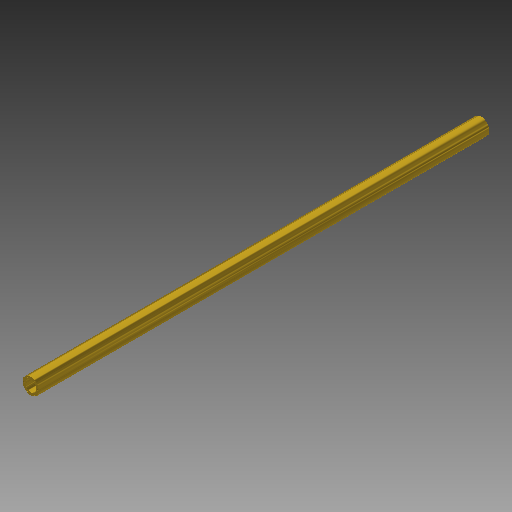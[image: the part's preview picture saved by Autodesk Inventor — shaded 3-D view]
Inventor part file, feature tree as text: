
AUTODESK INVENTOR PART (.ipt)
format: ipt  version: 2017 (Build 210142000, 142)  size: 137,728 bytes
history: native  units: mm (DEFAULTED — no unit token found)
features: revolve x2, pattern_circular x2, extrude x1, projected_geometry x1
ambient origin geometry x8: Origin, YZ Plane, XZ Plane, XY Plane, X Axis, Y Axis, Z Axis, Center Point
bodies: Solid1 (feature_tree)
feature tree (6):
  extrude  "Extrusion1"  Depth=12.7mm
  revolve  "Revolution2"  [1 undecoded]
  pattern_circular  "Circular Pattern1"  [2 undecoded]
  revolve  "Revolution3"  [1 undecoded]
  pattern_circular  "Circular Pattern2"  [2 undecoded]
  projected_geometry  "Projected Loop1"
note: 6 required parameter values undecoded (feature->parameter linkage not recoverable at this tier; creation-order binding heuristic only, values carry confidence <= 0.55)